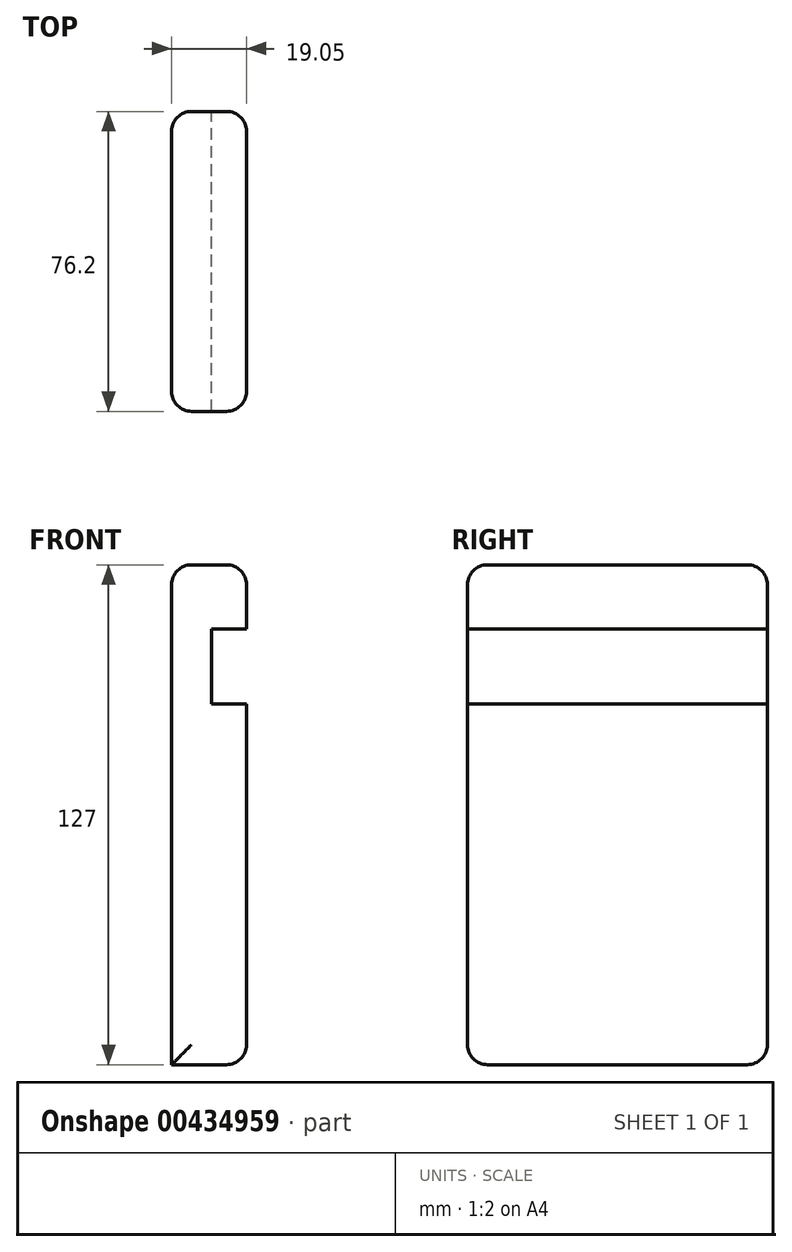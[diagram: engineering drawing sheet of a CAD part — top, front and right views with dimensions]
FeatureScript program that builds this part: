
annotation { "Feature Type Name" : "Feature", "Feature Type Description" : "" }
export const myFeature = defineFeature(function(context is Context, id is Id, definition is map)
    precondition{}
    {
        {
            var Q0;
            Q0=qCreatedBy(makeId("Front.planeOp"),FACE);
            var sketch = newSketch(context, id + "F0", { "sketchPlane" : qUnion([Q0])});
            skLineSegment(sketch, "E0.bottom", {"start": v(-70.84, -53.47) * mm, "end": v(-51.8, -53.47) * mm});
            skLineSegment(sketch, "E0.top", {"start": v(-70.84, 73.53) * mm, "end": v(-51.8, 73.53) * mm});
            skLineSegment(sketch, "E0.left", {"start": v(-70.84, -53.47) * mm, "end": v(-70.84, 73.53) * mm});
            skLineSegment(sketch, "E0.right", {"start": v(-51.8, -53.47) * mm, "end": v(-51.8, 73.53) * mm});
            skSolve(sketch);
        }
        {
            var Q0;
            Q0 = qSketchRegion(id + "F0", true);
            extrude(context, id + "F1", {"entities" : qUnion([Q0]), "depth" : 76.2 * mm});
        }
        {
            var Q0;
            Q0=makeQuery(id+"F1.opExtrude","SWEPT_FACE",FACE,{"disambiguationData":[OSD([sQuery(id+"F0.wireOp",EDGE,"E0.right")])]});
            var sketch = newSketch(context, id + "F2", { "sketchPlane" : qUnion([Q0])});
            skLineSegment(sketch, "E1.bottom", {"start": v(-76.2, 57.24) * mm, "end": v(0, 57.24) * mm});
            skLineSegment(sketch, "E1.top", {"start": v(-76.2, 38.2) * mm, "end": v(0, 38.2) * mm});
            skLineSegment(sketch, "E1.left", {"start": v(-76.2, 57.24) * mm, "end": v(-76.2, 38.2) * mm});
            skLineSegment(sketch, "E1.right", {"start": v(0, 57.24) * mm, "end": v(0, 38.2) * mm});
            skSolve(sketch);
        }
        {
            var Q0;
            Q0=makeQuery(id+"F2.imprint","IMPRINT",FACE,{"disambiguationData":[TD([[makeQuery(id+"F2.imprint","IMPRINT",EDGE,{"derivedFrom":sQuery(id+"F2.wireOp",EDGE,"E1.bottom")}),-1.0]])]});
            extrude(context, id + "F3", {"entities" : qUnion([Q0]), "operationType" : NewBodyOperationType.REMOVE, "oppositeDirection" : true, "depth" : 8.9 * mm});
        }
        {
            var Q0;
            Q0=makeQuery(id+"F1.opExtrude","CAP_EDGE",EDGE,{"disambiguationData":[OSD([sQuery(id+"F0.wireOp",EDGE,"E0.left")])],"isStart":false});
            var Q1;
            {var subQ0=sQuery(id+"F0.wireOp",EDGE,"E0.right");var subQ1=sQuery(id+"F0.wireOp",EDGE,"E0.top");Q1=makeQuery(id+"F3.boolean.opBoolean","SPLIT",EDGE,{"disambiguationData":[TD([makeQuery(id+"F1.opExtrude","SWEPT_FACE",FACE,{"disambiguationData":[OSD([subQ1])]})])],"derivedFrom":makeQuery(id+"F1.opExtrude","CAP_EDGE",EDGE,{"disambiguationData":[OSD([subQ0])],"isStart":false})});}
            var Q2;
            Q2=makeQuery(id+"F1.opExtrude","CAP_EDGE",EDGE,{"disambiguationData":[OSD([sQuery(id+"F0.wireOp",EDGE,"E0.top")])],"isStart":false});
            var Q3;
            Q3=makeQuery(id+"F3.boolean.opBoolean","COPY",EDGE,{"derivedFrom":makeQuery(id+"F3.opExtrude","CAP_EDGE",EDGE,{"disambiguationData":[OSD([sQuery(id+"F2.wireOp",EDGE,"E1.left")])],"isStart":false})});
            var Q4;
            Q4=makeQuery(id+"F3.boolean.opBoolean","COPY",EDGE,{"derivedFrom":makeQuery(id+"F3.opExtrude","CAP_EDGE",EDGE,{"disambiguationData":[OSD([sQuery(id+"F2.wireOp",EDGE,"E1.right")])],"isStart":false})});
            var Q5;
            {var subQ0=sQuery(id+"F0.wireOp",EDGE,"E0.bottom");var subQ1=sQuery(id+"F0.wireOp",EDGE,"E0.right");Q5=makeQuery(id+"F3.boolean.opBoolean","SPLIT",EDGE,{"disambiguationData":[TD([makeQuery(id+"F1.opExtrude","SWEPT_FACE",FACE,{"disambiguationData":[OSD([subQ0])]})])],"derivedFrom":makeQuery(id+"F1.opExtrude","CAP_EDGE",EDGE,{"disambiguationData":[OSD([subQ1])],"isStart":false})});}
            var Q6;
            Q6=makeQuery(id+"F1.opExtrude","SWEPT_EDGE",EDGE,{"disambiguationData":[OSD([sQuery(id+"F0.wireOp",EDGE,"E0.bottom"),sQuery(id+"F0.wireOp",EDGE,"E0.right")])]});
            var Q7;
            Q7=makeQuery(id+"F1.opExtrude","CAP_EDGE",EDGE,{"disambiguationData":[OSD([sQuery(id+"F0.wireOp",EDGE,"E0.bottom")])],"isStart":false});
            var Q8;
            Q8=makeQuery(id+"F1.opExtrude","CAP_EDGE",EDGE,{"disambiguationData":[OSD([sQuery(id+"F0.wireOp",EDGE,"E0.bottom")])],"isStart":true});
            var Q9;
            {var subQ0=sQuery(id+"F0.wireOp",EDGE,"E0.bottom");var subQ1=sQuery(id+"F0.wireOp",EDGE,"E0.right");Q9=makeQuery(id+"F3.boolean.opBoolean","SPLIT",EDGE,{"disambiguationData":[TD([makeQuery(id+"F1.opExtrude","SWEPT_FACE",FACE,{"disambiguationData":[OSD([subQ0])]})])],"derivedFrom":makeQuery(id+"F1.opExtrude","CAP_EDGE",EDGE,{"disambiguationData":[OSD([subQ1])],"isStart":true})});}
            var Q10;
            Q10=makeQuery(id+"F1.opExtrude","CAP_EDGE",EDGE,{"disambiguationData":[OSD([sQuery(id+"F0.wireOp",EDGE,"E0.left")])],"isStart":true});
            var Q11;
            {var subQ0=sQuery(id+"F0.wireOp",EDGE,"E0.right");var subQ1=sQuery(id+"F0.wireOp",EDGE,"E0.top");Q11=makeQuery(id+"F3.boolean.opBoolean","SPLIT",EDGE,{"disambiguationData":[TD([makeQuery(id+"F1.opExtrude","SWEPT_FACE",FACE,{"disambiguationData":[OSD([subQ1])]})])],"derivedFrom":makeQuery(id+"F1.opExtrude","CAP_EDGE",EDGE,{"disambiguationData":[OSD([subQ0])],"isStart":true})});}
            var Q12;
            Q12=makeQuery(id+"F1.opExtrude","CAP_EDGE",EDGE,{"disambiguationData":[OSD([sQuery(id+"F0.wireOp",EDGE,"E0.top")])],"isStart":true});
            var Q13;
            Q13=makeQuery(id+"F1.opExtrude","SWEPT_EDGE",EDGE,{"disambiguationData":[OSD([sQuery(id+"F0.wireOp",EDGE,"E0.top"),sQuery(id+"F0.wireOp",EDGE,"E0.right")])]});
            var Q14;
            Q14=makeQuery(id+"F1.opExtrude","SWEPT_EDGE",EDGE,{"disambiguationData":[OSD([sQuery(id+"F0.wireOp",EDGE,"E0.top"),sQuery(id+"F0.wireOp",EDGE,"E0.left")])]});
            fillet(context, id + "F4", {"entities" : qUnion([Q0, Q1, Q2, Q3, Q4, Q5, Q6, Q7, Q8, Q9, Q10, Q11, Q12, Q13, Q14]), "radius" : 5.08 * mm, "tangentPropagation" : true, "allowEdgeOverflow" : false});
        }
    });
